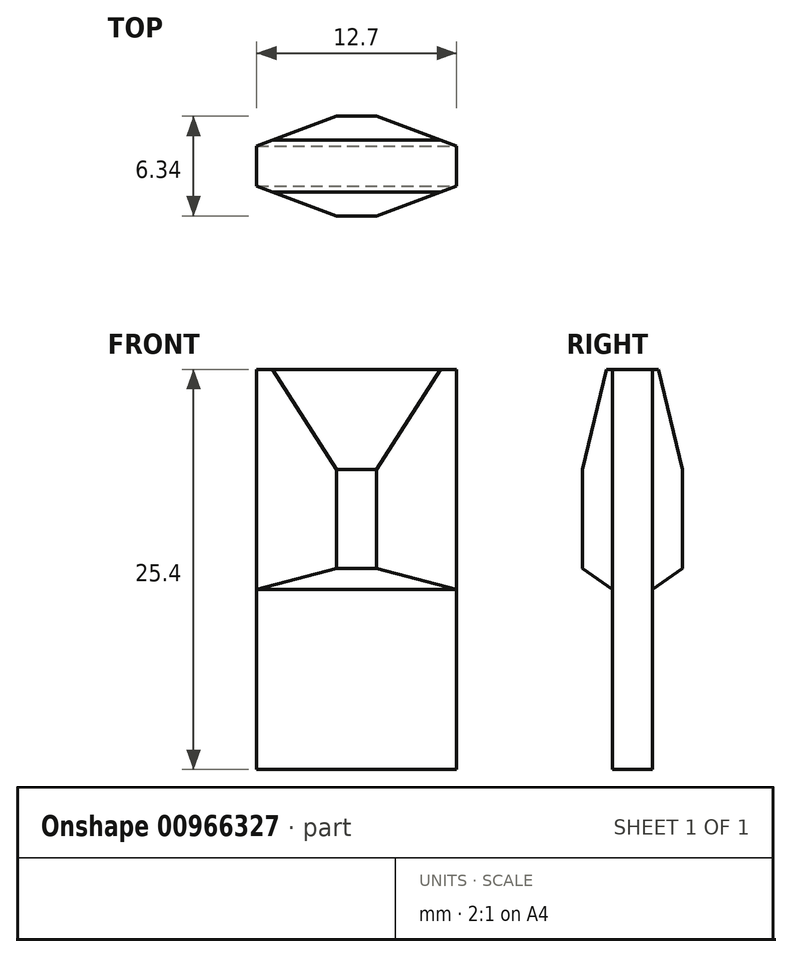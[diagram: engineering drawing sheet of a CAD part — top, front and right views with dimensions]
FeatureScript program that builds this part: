
annotation { "Feature Type Name" : "Feature", "Feature Type Description" : "" }
export const myFeature = defineFeature(function(context is Context, id is Id, definition is map)
    precondition{}
    {
        {
            var Q0;
            Q0=qCreatedBy(makeId("Top.planeOp"),FACE);
            var sketch = newSketch(context, id + "F0", { "sketchPlane" : qUnion([Q0])});
            skLineSegment(sketch, "E0.top", {"start": v(-1.27, 3.17) * mm, "end": v(1.27, 3.17) * mm});
            skLineSegment(sketch, "E0.left", {"start": v(-6.35, 0) * mm, "end": v(-6.35, 1.27) * mm});
            skLineSegment(sketch, "E0.right", {"start": v(6.35, 0) * mm, "end": v(6.35, 1.27) * mm});
            skLineSegment(sketch, "E1", {"start": v(-6.35, 1.27) * mm, "end": v(-1.27, 3.18) * mm});
            skLineSegment(sketch, "E2.MirrorCS", {"start": v(6.35, 1.27) * mm, "end": v(1.27, 3.18) * mm});
            skLineSegment(sketch, "E3.MirrorCS", {"start": v(6.35, 0) * mm, "end": v(6.35, -1.27) * mm});
            skLineSegment(sketch, "E4.MirrorCS", {"start": v(6.35, -1.27) * mm, "end": v(1.27, -3.18) * mm});
            skLineSegment(sketch, "E5.MirrorCS", {"start": v(-1.27, -3.17) * mm, "end": v(1.27, -3.17) * mm});
            skLineSegment(sketch, "E6.MirrorCS", {"start": v(-6.35, -1.27) * mm, "end": v(-1.27, -3.18) * mm});
            skLineSegment(sketch, "E7.MirrorCS", {"start": v(-6.35, 0) * mm, "end": v(-6.35, -1.27) * mm});
            skSolve(sketch);
        }
        {
            var Q0;
            Q0 = qSketchRegion(id + "F0", true);
            extrude(context, id + "F1", {"entities" : qUnion([Q0]), "endBound" : BoundingType.SYMMETRIC, "depth" : 25.4 * mm, "offsetDistance" : 25.4 * mm});
        }
        {
            var Q0;
            Q0=qCreatedBy(makeId("Right.planeOp"),FACE);
            var sketch = newSketch(context, id + "F2", { "sketchPlane" : qUnion([Q0])});
            skLineSegment(sketch, "E8", {"start": v(-1.65, 12.7) * mm, "end": v(-3.17, 6.35) * mm});
            skLineSegment(sketch, "E9", {"start": v(-3.18, 6.35) * mm, "end": v(-3.18, 12.7) * mm});
            skLineSegment(sketch, "E10", {"start": v(-3.18, 12.7) * mm, "end": v(-1.65, 12.7) * mm});
            skLineSegment(sketch, "E11", {"start": v(1.65, 12.7) * mm, "end": v(3.18, 6.35) * mm});
            skLineSegment(sketch, "E12", {"start": v(3.18, 6.35) * mm, "end": v(3.18, 12.7) * mm});
            skLineSegment(sketch, "E13", {"start": v(3.18, 12.7) * mm, "end": v(1.65, 12.7) * mm});
            skLineSegment(sketch, "E14", {"start": v(-4.5, 1) * mm, "end": v(-1.27, -1.27) * mm});
            skLineSegment(sketch, "E15", {"start": v(-1.27, -1.27) * mm, "end": v(-1.27, -17.61) * mm});
            skLineSegment(sketch, "E16", {"start": v(-1.27, -17.61) * mm, "end": v(-4.5, -17.61) * mm});
            skLineSegment(sketch, "E17", {"start": v(-4.5, -17.61) * mm, "end": v(-4.5, 1) * mm});
            skLineSegment(sketch, "E18.MirrorCS", {"start": v(4.5, -17.61) * mm, "end": v(4.5, 1) * mm});
            skLineSegment(sketch, "E19.MirrorCS", {"start": v(1.27, -17.61) * mm, "end": v(4.5, -17.61) * mm});
            skLineSegment(sketch, "E20.MirrorCS", {"start": v(1.27, -1.27) * mm, "end": v(1.27, -17.61) * mm});
            skLineSegment(sketch, "E21.MirrorCS", {"start": v(4.5, 1) * mm, "end": v(1.27, -1.27) * mm});
            skSolve(sketch);
        }
        {
            var Q0;
            Q0 = qSketchRegion(id + "F2", true);
            extrude(context, id + "F3", {"entities" : qUnion([Q0]), "operationType" : NewBodyOperationType.REMOVE, "endBound" : BoundingType.SYMMETRIC, "oppositeDirection" : true, "depth" : 50.8 * mm, "offsetDistance" : 25.4 * mm});
        }
    });
